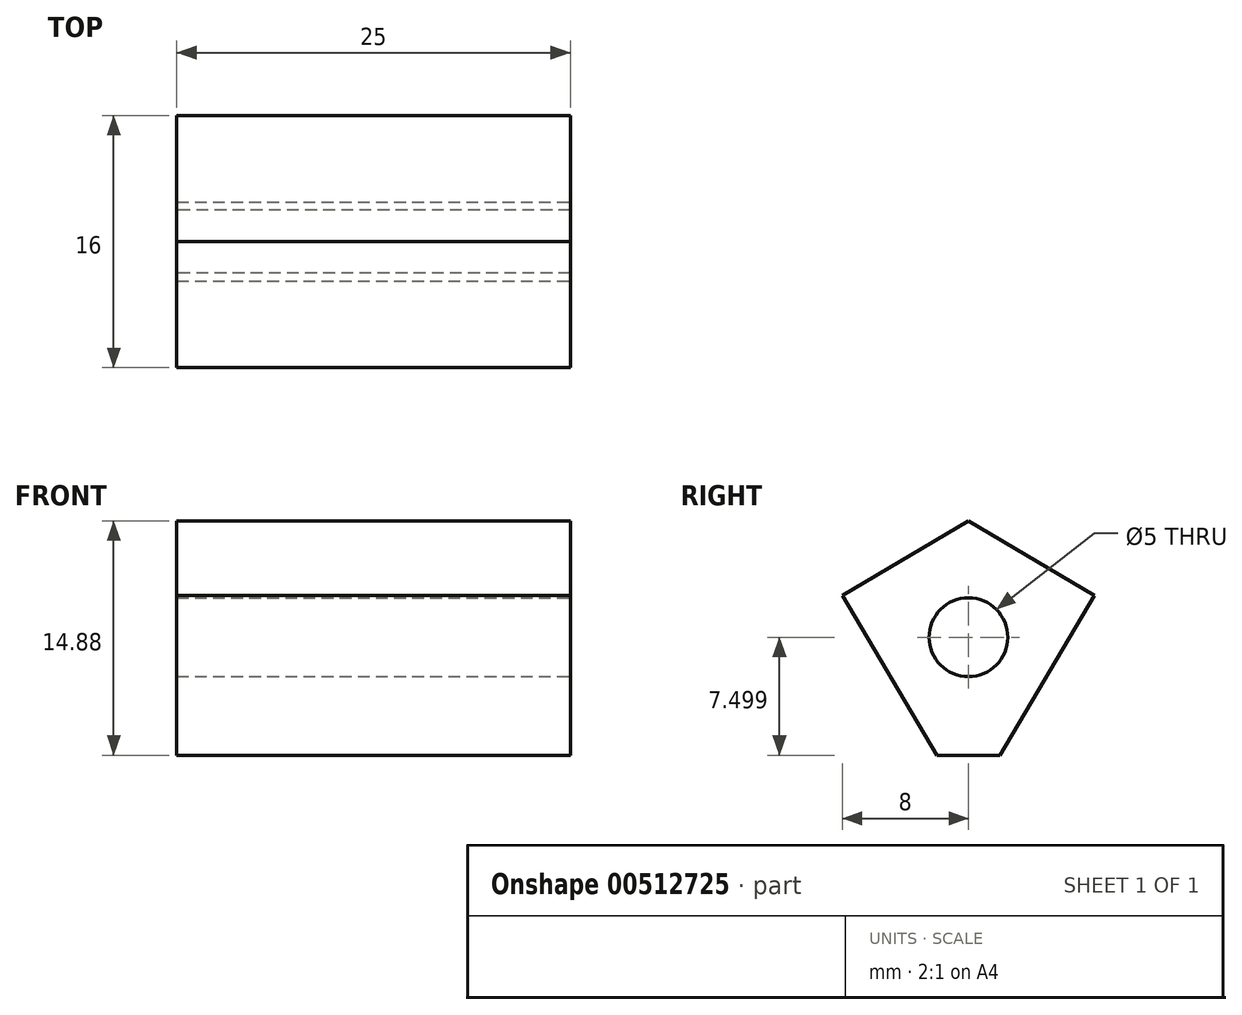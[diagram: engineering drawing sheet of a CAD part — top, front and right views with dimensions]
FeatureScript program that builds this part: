
annotation { "Feature Type Name" : "Feature", "Feature Type Description" : "" }
export const myFeature = defineFeature(function(context is Context, id is Id, definition is map)
    precondition{}
    {
        {
            var Q0;
            Q0=qCreatedBy(makeId("Right.planeOp"),FACE);
            var sketch = newSketch(context, id + "F0", { "sketchPlane" : qUnion([Q0])});
            skLineSegment(sketch, "E0", {"start": v(2, -10.16) * mm, "end": v(-2, -10.16) * mm});
            skLineSegment(sketch, "E1", {"start": v(-2, -10.16) * mm, "end": v(-8, 0) * mm});
            skLineSegment(sketch, "E2", {"start": v(-8, 0) * mm, "end": v(0, 4.72) * mm});
            skLineSegment(sketch, "E3", {"start": v(0, 4.72) * mm, "end": v(8, 0) * mm});
            skLineSegment(sketch, "E4", {"start": v(8, 0) * mm, "end": v(2, -10.16) * mm});
            skSolve(sketch);
        }
        {
            var Q0;
            Q0 = qSketchRegion(id + "F0", true);
            extrude(context, id + "F1", {"entities" : qUnion([Q0]), "depth" : 25 * mm});
        }
        {
            var Q0;
            Q0=makeQuery(id+"F1.opExtrude","CAP_FACE",FACE,{"disambiguationData":[OSD([sQuery(id+"F0.wireOp",EDGE,"E0"),sQuery(id+"F0.wireOp",EDGE,"E1"),sQuery(id+"F0.wireOp",EDGE,"E2"),sQuery(id+"F0.wireOp",EDGE,"E3"),sQuery(id+"F0.wireOp",EDGE,"E4")])],"isStart":false});
            var sketch = newSketch(context, id + "F2", { "sketchPlane" : qUnion([Q0])});
            skCircle(sketch, "E5", {"center": v(0, -2.66) * mm, "radius": 2.5 * mm});
            skSolve(sketch);
        }
        {
            var Q0;
            Q0=sQuery(id+"F2.wireOp",VERTEX,"E5.center");
            var Q1;
            Q1=makeQuery(id+"F1.opExtrude","SWEPT_BODY",BODY,{"disambiguationData":[OSD([sQuery(id+"F0.wireOp",EDGE,"E0"),sQuery(id+"F0.wireOp",EDGE,"E1"),sQuery(id+"F0.wireOp",EDGE,"E2"),sQuery(id+"F0.wireOp",EDGE,"E3"),sQuery(id+"F0.wireOp",EDGE,"E4")])]});
            hole(context, id + "F3", {"style" : HoleStyle.SIMPLE, "endStyle" : HoleEndStyle.THROUGH, "holeDiameter" : 5 * mm, "isTappedThrough" : true, "tappedDepth" : 12 * mm, "tapClearance" : 3, "locations" : qUnion([Q0]), "scope" : qUnion([Q1])});
        }
    });
